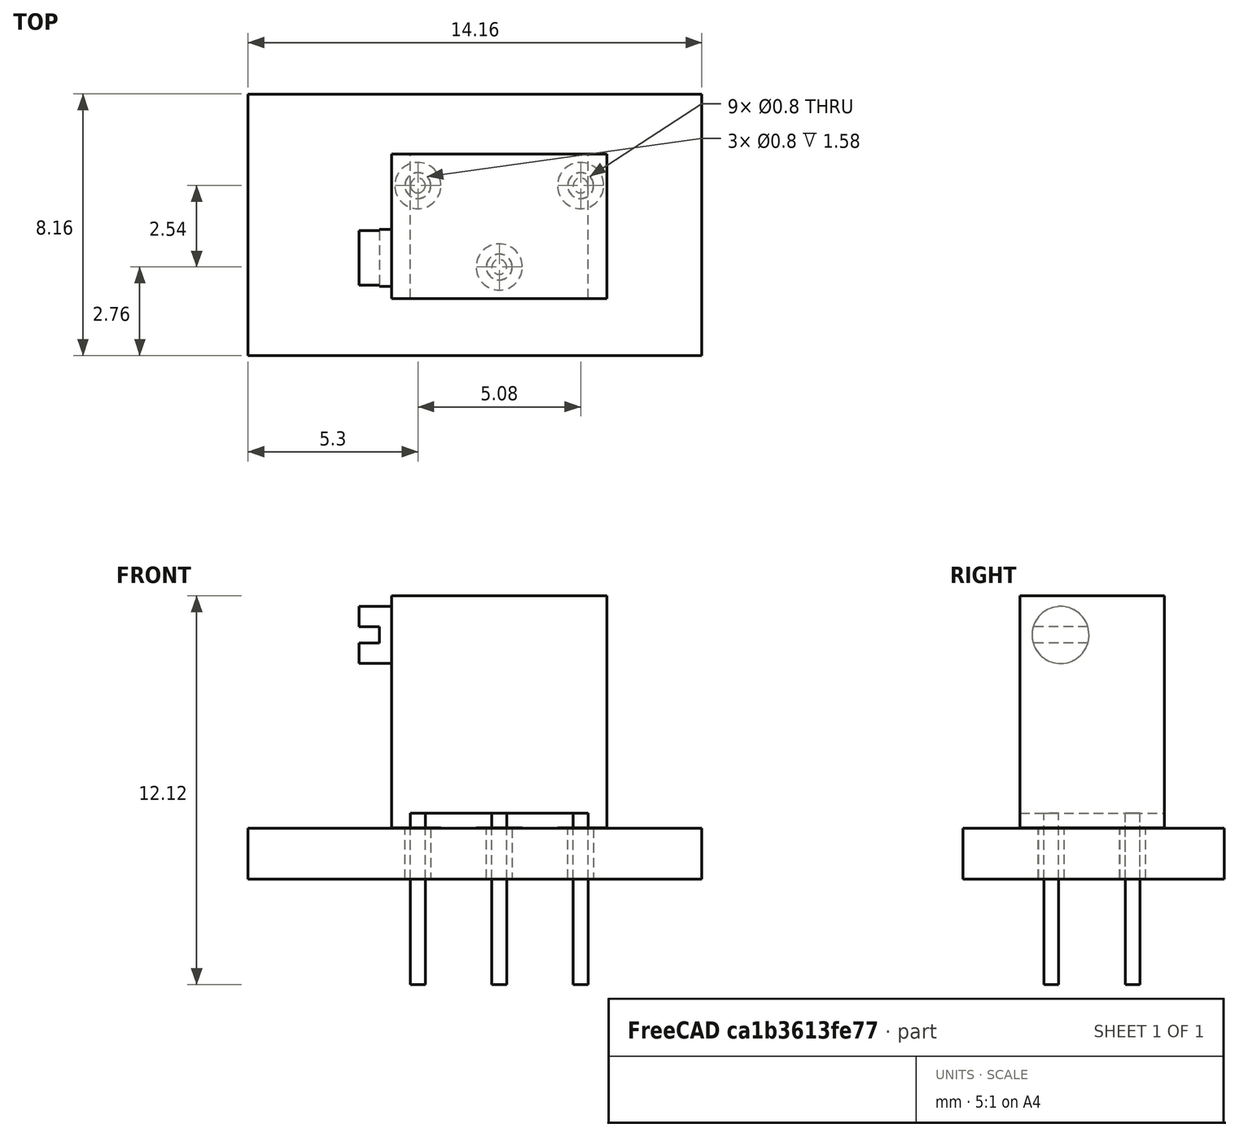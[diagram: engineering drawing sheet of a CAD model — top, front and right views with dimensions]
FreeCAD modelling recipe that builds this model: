
FCSTD DOCUMENT  (FreeCAD 0.18R15611 (Git))
Label: Potentiometer_Bourns_3266X_Horizontal
License: All rights reserved
LicenseURL: http://en.wikipedia.org/wiki/All_rights_reserved
objects: Part::FeaturePython×7, Part::Cylinder×4, Part::Box×4, Part::MultiFuse×2, App::DocumentObjectGroup×1, Part::Cut×1, Part::Feature×1
note: 19 computed .brp shape members not serialized (recipe doc carries the construction recipe); baked Part::Feature solids carry a one-line shape summary decoded from their .brp

FEATURE [Part::FeaturePython] FCrtYd_lines  label="FCrtYd"  # a2plus imported part (geometry in sourceFile) (typed FeaturePython)
  fixedPosition = true
FEATURE [Part::FeaturePython] FFab_lines  label="FFab"  # a2plus imported part (geometry in sourceFile) (typed FeaturePython)
  fixedPosition = true
FEATURE [Part::FeaturePython] Filk_lines  label="FrontSilk"  # a2plus imported part (geometry in sourceFile) (typed FeaturePython)
  fixedPosition = true
FEATURE [Part::FeaturePython] TopPads  # a2plus imported part (geometry in sourceFile) (typed FeaturePython)
  fixedPosition = true
FEATURE [Part::FeaturePython] BotPads  # a2plus imported part (geometry in sourceFile) (typed FeaturePython)
  fixedPosition = true
FEATURE [Part::FeaturePython] THPs  label="PTHs"  # a2plus imported part (geometry in sourceFile) (typed FeaturePython)
  fixedPosition = true
FEATURE [Part::FeaturePython] newPCB  label="Pcb"  # a2plus imported part (geometry in sourceFile) (typed FeaturePython)
  fixedPosition = true
FEATURE [App::DocumentObjectGroup] Potentiometer_Bourns_3266X_Horizontal_fp
  Group = -> [FCrtYd_lines,FFab_lines,Filk_lines,TopPads,BotPads,THPs,newPCB]
FEATURE [Part::Cylinder] Cylinder001  label="Pin3"
  Angle = 360
  AttacherType = Attacher::AttachEngine3D
  Height = 5.34
  Placement = pos=(-5.08,0,-4.88) rot=(0,0,1;0rad)
  Radius = 0.23
FEATURE [Part::Cylinder] Cylinder002  label="Pin2"
  Angle = 360
  AttacherType = Attacher::AttachEngine3D
  Height = 5.34
  Placement = pos=(-2.54,-2.54,-4.88) rot=(0,0,1;0rad)
  Radius = 0.23
FEATURE [Part::Cylinder] Cylinder  label="Pin1"
  Angle = 360
  AttacherType = Attacher::AttachEngine3D
  Height = 5.34
  Placement = pos=(0,0,-4.88) rot=(0,0,1;0rad)
  Radius = 0.23
FEATURE [Part::Box] Box  label="Body"
  AttacherType = Attacher::AttachEngine3D
  Height = 6.78
  Length = 6.71
  Placement = pos=(-5.895,-3.52,0.46) rot=(0,0,1;0rad)
  Width = 4.5
FEATURE [Part::Box] Box001  label="Standoff1"
  AttacherType = Attacher::AttachEngine3D
  Height = 0.46
  Length = 0.585
  Placement = pos=(0.23,-3.52,0) rot=(0,0,1;0rad)
  Width = 4.5
FEATURE [Part::Box] Box002  label="Standoff2"
  AttacherType = Attacher::AttachEngine3D
  Height = 0.46
  Length = 0.585
  Placement = pos=(-5.895,-3.52,0) rot=(0,0,1;0rad)
  Width = 4.5
FEATURE [Part::MultiFuse] Fusion  label="FusionBody"
  Refine = true
  Shapes = -> [Box,Box001,Box002]
FEATURE [Part::Cylinder] Cylinder003  label="Knob"
  Angle = 360
  AttacherType = Attacher::AttachEngine3D
  Height = 1.02
  Placement = pos=(-0.405,-2.25,7.24) rot=(0,0,1;0rad)
  Radius = 0.89
FEATURE [Part::Box] Box003  label="Cube"
  AttacherType = Attacher::AttachEngine3D
  Height = 0.64
  Length = 10
  Placement = pos=(-5,-2.5,7.62) rot=(0,0,1;0rad)
  Width = 0.51
FEATURE [Part::Cut] Cut  label="CutKnob"
  Base = -> Cylinder003
  Placement = pos=(1.345,-2.66,8.27) rot=(0.57735,-0.57735,-0.57735;2.0944rad)
  Refine = true
  Tool = -> Box003
FEATURE [Part::MultiFuse] Pin2_mp_cp  label="Pin2_fd"
  Refine = true
  Shapes = -> [Cylinder002,Cylinder001,Fusion,Cut,Cylinder]
FEATURE [Part::Feature] Shape  label="Potentiometer_Bourns_3266X_Horizontal"
  shape: bbox 7.73 x 4.5 x 12.12 mm, 22 faces (baked)
